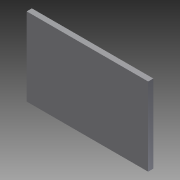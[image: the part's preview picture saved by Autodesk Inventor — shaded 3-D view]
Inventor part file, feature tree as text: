
AUTODESK INVENTOR PART (.ipt)
format: ipt  version: 2012 SP2 (Build 160219200, 219)  size: 87,040 bytes
history: native  units: in
note: dims shown in document units (in); Inventor stores cm internally (conversion verified against a paired STEP export)
features: extrude x3, sketch x3
ambient origin geometry x8: Origin, YZ Plane, XZ Plane, XY Plane, X Axis, Y Axis, Z Axis, Center Point
bodies: Solid1 (feature_tree)
feature tree (6):
  extrude  "Extrusion1"  Depth=0.5906in
  extrude  "Extrusion2"  Depth=6.2992in
  extrude  "Extrusion3"  [1 undecoded]
  sketch  "Sketch1"  dims[d0=1.1811in d1=0.0in d2=0.5906in]
  sketch  "Sketch2"  dims[d3=0.1181in d4=0.0in d5=6.2992in]
  sketch  "Sketch3"  dims[d6=0.9306in d7=0.0in]
note: 1 required parameter value undecoded (feature->parameter linkage not recoverable at this tier; creation-order binding heuristic only, values carry confidence <= 0.55)
